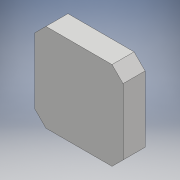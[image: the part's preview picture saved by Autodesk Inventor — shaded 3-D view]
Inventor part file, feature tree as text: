
AUTODESK INVENTOR PART (.ipt)
format: ipt  version: 2018 (Build 220112000, 112)  size: 182,784 bytes
history: native  units: mm
features: extrude x2, chamfer x2, sketch x2
ambient origin geometry x8: Origin, YZ Plane, XZ Plane, XY Plane, X Axis, Y Axis, Z Axis, Center Point
bodies: Solide1 (feature_tree)
feature tree (6):
  extrude  "Extrusion1"  Depth=32.0mm
  extrude  "Extrusion2"  Depth=32.0mm
  chamfer  "Chanfrein1"  Distance=8.0mm
  chamfer  "Chanfrein2"  Distance=2.0mm
  sketch  "Esquisse1"
  sketch  "Esquisse2"
